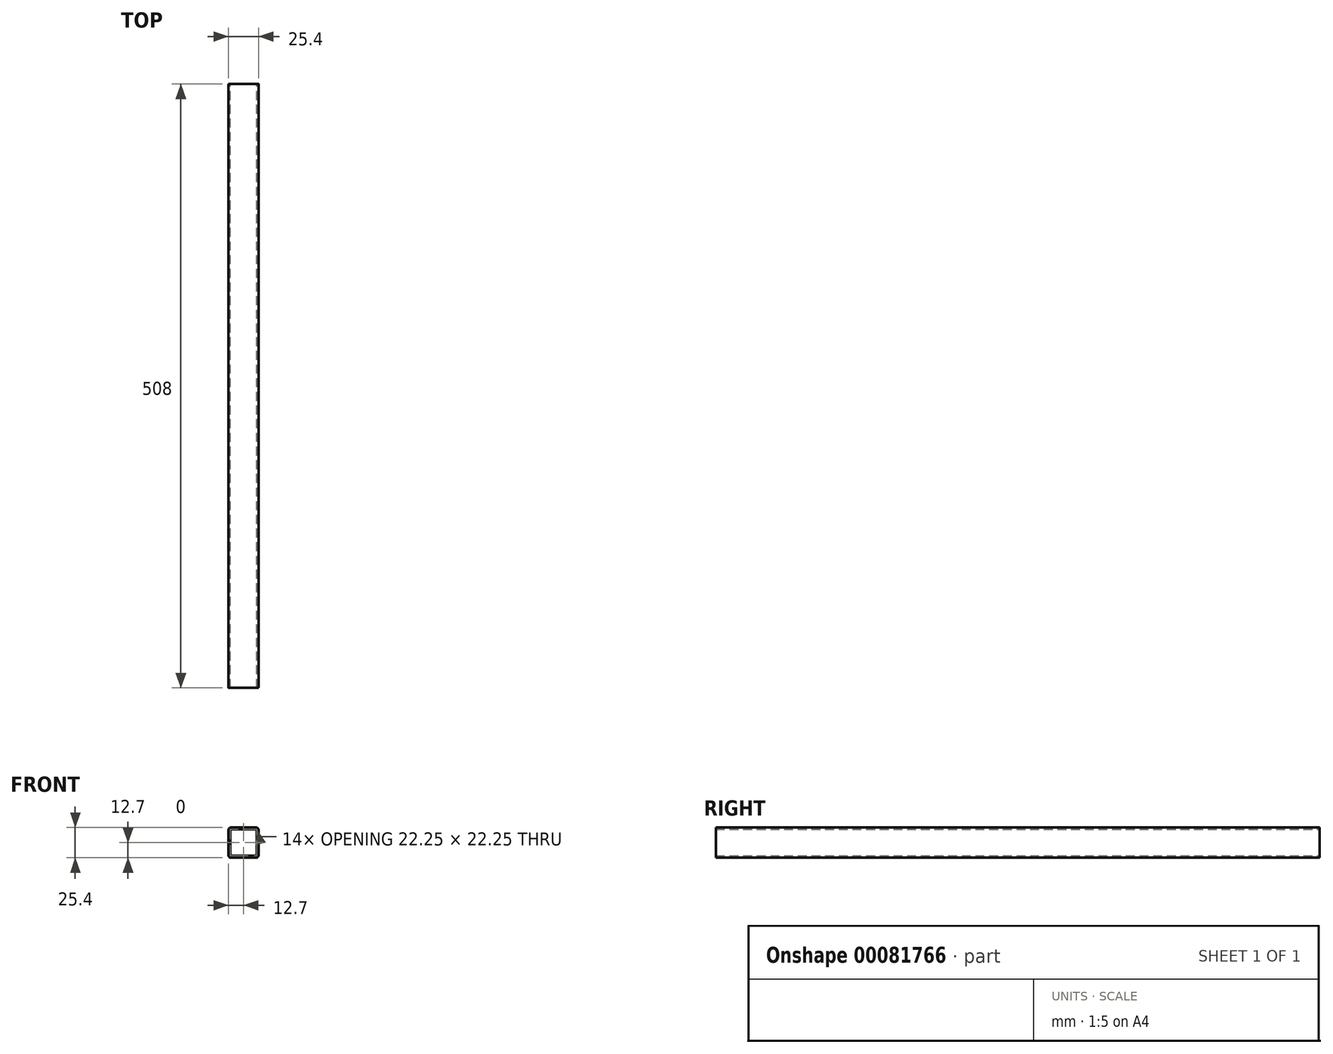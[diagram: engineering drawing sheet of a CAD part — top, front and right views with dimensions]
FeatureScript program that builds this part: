
annotation { "Feature Type Name" : "Feature", "Feature Type Description" : "" }
export const myFeature = defineFeature(function(context is Context, id is Id, definition is map)
    precondition{}
    {
        {
            var Q0;
            Q0=qCreatedBy(makeId("Front.planeOp"),FACE);
            var sketch = newSketch(context, id + "F0", { "sketchPlane" : qUnion([Q0])});
            skLineSegment(sketch, "E0.bottom", {"start": v(-10.62, -12.7) * mm, "end": v(10.62, -12.7) * mm});
            skLineSegment(sketch, "E0.top", {"start": v(-10.62, 12.7) * mm, "end": v(10.62, 12.7) * mm});
            skLineSegment(sketch, "E0.left", {"start": v(-12.7, -10.62) * mm, "end": v(-12.7, 10.62) * mm});
            skLineSegment(sketch, "E0.right", {"start": v(12.7, -10.62) * mm, "end": v(12.7, 10.62) * mm});
            skPoint(sketch, "E0.middle", {"position": v(0, 0) * mm});
            skLineSegment(sketch, "E1.bottom", {"start": v(10.62, -11.13) * mm, "end": v(-10.62, -11.13) * mm});
            skLineSegment(sketch, "E1.top", {"start": v(10.62, 11.13) * mm, "end": v(-10.62, 11.13) * mm});
            skLineSegment(sketch, "E1.left", {"start": v(11.13, -10.62) * mm, "end": v(11.13, 10.62) * mm});
            skLineSegment(sketch, "E1.right", {"start": v(-11.13, -10.62) * mm, "end": v(-11.13, 10.62) * mm});
            skPoint(sketch, "E2.visualSharp", {"position": v(-11.13, 11.13) * mm});
            skArc(sketch, "E2.filletArc", {"start": v(-10.62, 11.13) * mm, "mid": v(-10.98, 10.98) * mm, "end": v(-11.13, 10.62) * mm});
            skPoint(sketch, "E3.visualSharp", {"position": v(11.13, 11.13) * mm});
            skArc(sketch, "E3.filletArc", {"start": v(11.13, 10.62) * mm, "mid": v(10.98, 10.98) * mm, "end": v(10.62, 11.13) * mm});
            skPoint(sketch, "E4.visualSharp", {"position": v(11.13, -11.13) * mm});
            skArc(sketch, "E4.filletArc", {"start": v(10.62, -11.13) * mm, "mid": v(10.98, -10.98) * mm, "end": v(11.13, -10.62) * mm});
            skPoint(sketch, "E5.visualSharp", {"position": v(-11.13, -11.13) * mm});
            skArc(sketch, "E5.filletArc", {"start": v(-11.13, -10.62) * mm, "mid": v(-10.98, -10.98) * mm, "end": v(-10.62, -11.13) * mm});
            skPoint(sketch, "E6.visualSharp", {"position": v(-12.7, 12.7) * mm});
            skArc(sketch, "E6.filletArc", {"start": v(-10.62, 12.7) * mm, "mid": v(-12.09, 12.09) * mm, "end": v(-12.7, 10.62) * mm});
            skPoint(sketch, "E7.visualSharp", {"position": v(12.7, 12.7) * mm});
            skArc(sketch, "E7.filletArc", {"start": v(12.7, 10.62) * mm, "mid": v(12.09, 12.09) * mm, "end": v(10.62, 12.7) * mm});
            skPoint(sketch, "E8.visualSharp", {"position": v(-12.7, -12.7) * mm});
            skArc(sketch, "E8.filletArc", {"start": v(-12.7, -10.62) * mm, "mid": v(-12.09, -12.09) * mm, "end": v(-10.62, -12.7) * mm});
            skPoint(sketch, "E9.visualSharp", {"position": v(12.7, -12.7) * mm});
            skArc(sketch, "E9.filletArc", {"start": v(10.62, -12.7) * mm, "mid": v(12.09, -12.09) * mm, "end": v(12.7, -10.62) * mm});
            skSolve(sketch);
        }
        {
            var Q0;
            Q0 = qSketchRegion(id + "F0", true);
            extrude(context, id + "F1", {"entities" : qUnion([Q0]), "depth" : 508 * mm});
        }
    });
